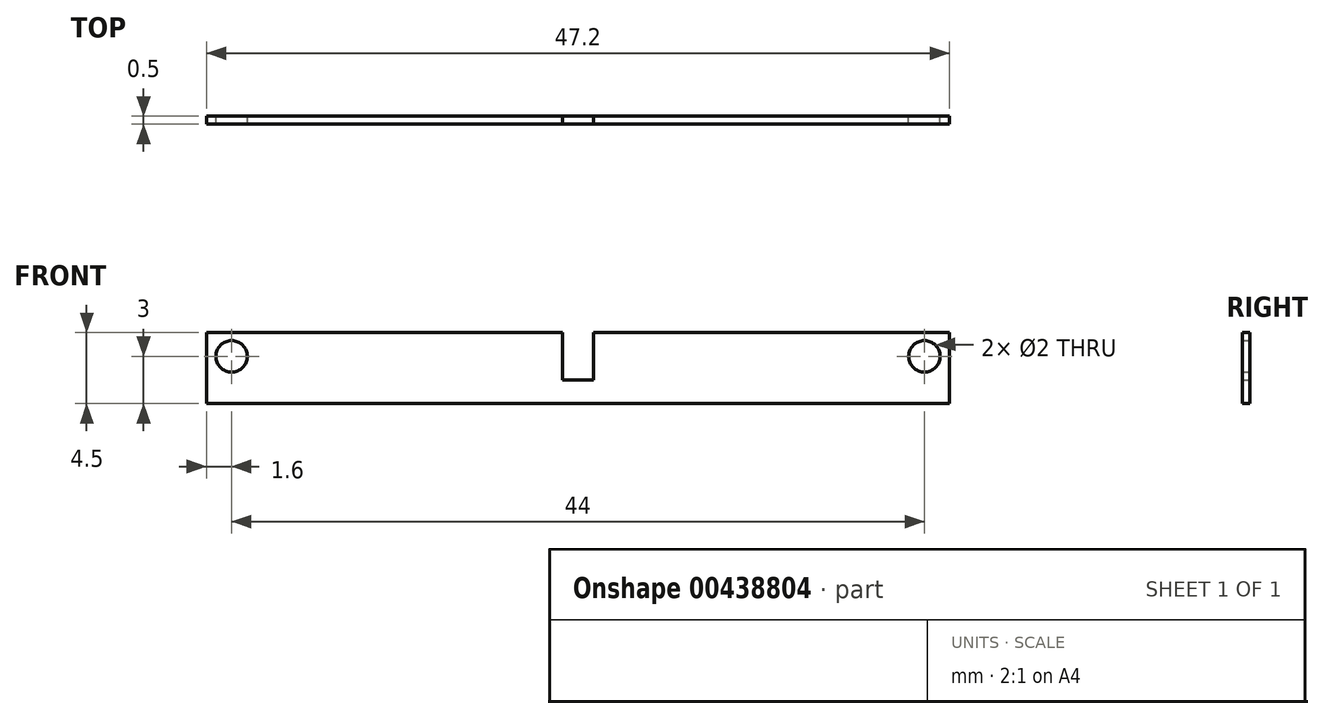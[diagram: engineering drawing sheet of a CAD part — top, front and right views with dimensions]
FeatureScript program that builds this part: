
annotation { "Feature Type Name" : "Feature", "Feature Type Description" : "" }
export const myFeature = defineFeature(function(context is Context, id is Id, definition is map)
    precondition{}
    {
        {
            var Q0;
            Q0=qCreatedBy(makeId("Front.planeOp"),FACE);
            var sketch = newSketch(context, id + "F0", { "sketchPlane" : qUnion([Q0])});
            skLineSegment(sketch, "E0.bottom", {"start": v(23.6, -2.25) * mm, "end": v(-23.6, -2.25) * mm});
            skLineSegment(sketch, "E0.top", {"start": v(23.6, 2.25) * mm, "end": v(1, 2.25) * mm});
            skLineSegment(sketch, "E0.left", {"start": v(23.6, -2.25) * mm, "end": v(23.6, 2.25) * mm});
            skLineSegment(sketch, "E0.right", {"start": v(-23.6, -2.25) * mm, "end": v(-23.6, 2.25) * mm});
            skPoint(sketch, "E0.middle", {"position": v(0, 0) * mm});
            skLineSegment(sketch, "E1.bottom", {"start": v(1, -0.75) * mm, "end": v(-1, -0.75) * mm});
            skLineSegment(sketch, "E1.left", {"start": v(1, -0.75) * mm, "end": v(1, 2.25) * mm});
            skLineSegment(sketch, "E1.right", {"start": v(-1, -0.75) * mm, "end": v(-1, 2.25) * mm});
            skLineSegment(sketch, "E2.trimOffspring", {"start": v(-1, 2.25) * mm, "end": v(-23.6, 2.25) * mm});
            skCircle(sketch, "E3", {"center": v(-22, 0.75) * mm, "radius": 1 * mm});
            skCircle(sketch, "E4.MirrorC", {"center": v(22, 0.75) * mm, "radius": 1 * mm});
            skSolve(sketch);
        }
        {
            var Q0;
            Q0 = qSketchRegion(id + "F0", true);
            extrude(context, id + "F1", {"entities" : qUnion([Q0]), "depth" : .5 * mm});
        }
    });
